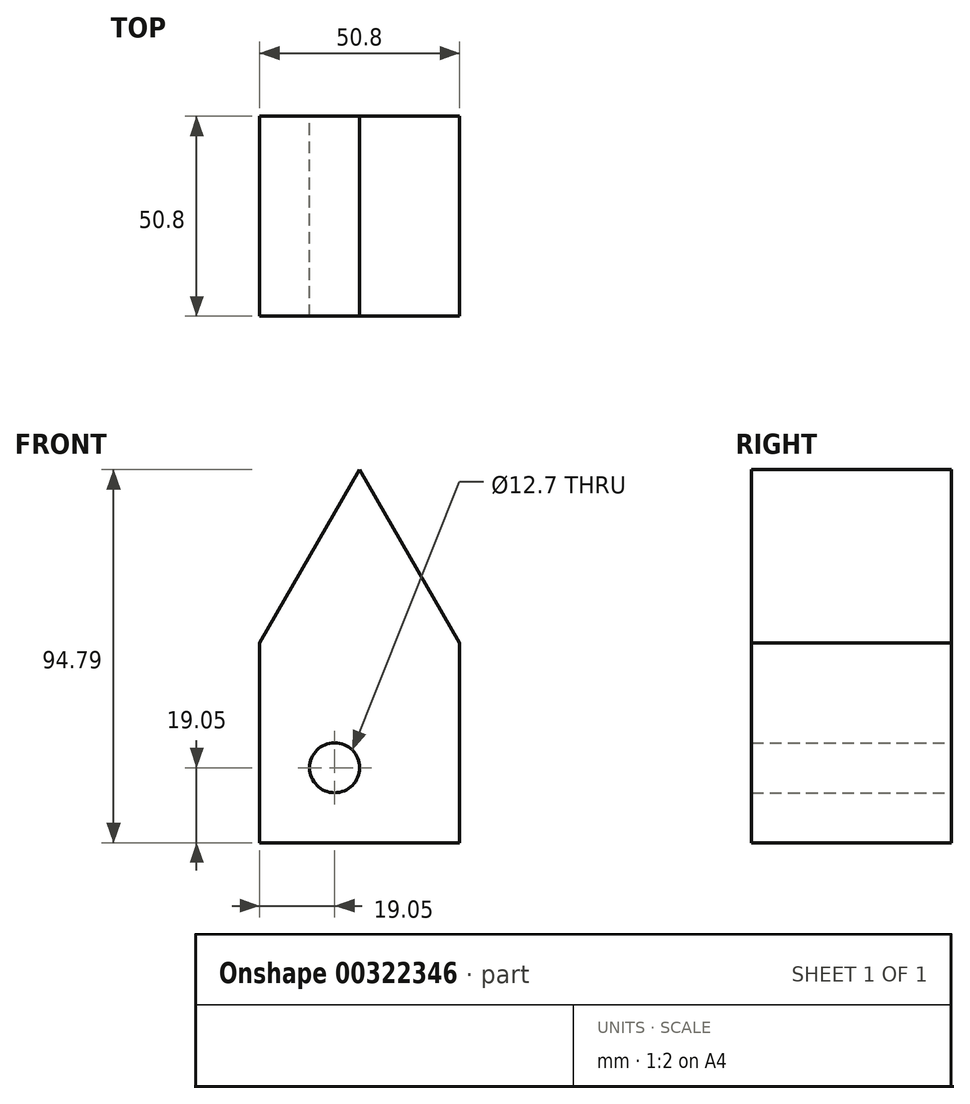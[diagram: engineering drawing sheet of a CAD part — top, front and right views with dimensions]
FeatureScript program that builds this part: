
annotation { "Feature Type Name" : "Feature", "Feature Type Description" : "" }
export const myFeature = defineFeature(function(context is Context, id is Id, definition is map)
    precondition{}
    {
        {
            var Q0;
            Q0=qCreatedBy(makeId("Front.planeOp"),FACE);
            var sketch = newSketch(context, id + "F0", { "sketchPlane" : qUnion([Q0])});
            skLineSegment(sketch, "E0.top", {"start": v(-25.4, -25.4) * mm, "end": v(25.4, -25.4) * mm});
            skLineSegment(sketch, "E0.left", {"start": v(-25.4, 25.4) * mm, "end": v(-25.4, -25.4) * mm});
            skLineSegment(sketch, "E0.right", {"start": v(25.4, 25.4) * mm, "end": v(25.4, -25.4) * mm});
            skPoint(sketch, "E0.middle", {"position": v(0, 0) * mm});
            skLineSegment(sketch, "E1", {"start": v(-25.4, 25.4) * mm, "end": v(0, 69.4) * mm});
            skLineSegment(sketch, "E2", {"start": v(25.4, 25.4) * mm, "end": v(0, 69.4) * mm});
            skCircle(sketch, "E3", {"center": v(-6.35, -6.35) * mm, "radius": 6.35 * mm});
            skSolve(sketch);
        }
        {
            var Q0;
            Q0=makeQuery(id+"F0.imprint","IMPRINT",FACE,{"disambiguationData":[TD([[makeQuery(id+"F0.imprint","IMPRINT",EDGE,{"derivedFrom":sQuery(id+"F0.wireOp",EDGE,"E0.top")}),1.0]])]});
            extrude(context, id + "F1", {"entities" : qUnion([Q0]), "depth" : 50.8 * mm});
        }
    });
